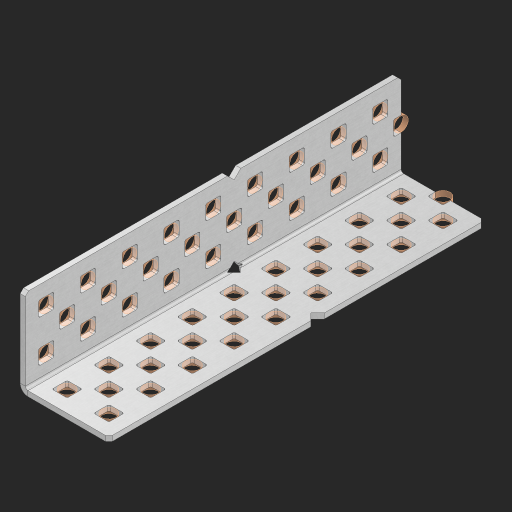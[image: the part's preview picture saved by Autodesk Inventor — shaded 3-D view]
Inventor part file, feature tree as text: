
AUTODESK INVENTOR PART (.ipt)
format: ipt  version: 2023 (Build 270158000, 158)  size: 940,544 bytes
history: native  units: in
note: dims shown in document units (in); Inventor stores cm internally (conversion verified against a paired STEP export)
features: other x60, extrude x52, sheet_metal_op x8, sketch x7, pattern_linear x2, mirror x1, chamfer x1
ambient origin geometry x8: Origin, YZ Plane, XZ Plane, XY Plane, X Axis, Y Axis, Z Axis, Center Point
bodies: Solid1 (feature_tree), Body (feature_tree)
feature tree (131):
  sheet_metal_op  "Flanges"
  sheet_metal_op  "Body Pattern"
  pattern_linear  "Center Pattern"  Spacing1=1.0in  [1 undecoded]
  other  "Arc Length"
  pattern_linear  "Notch Pattern"  Spacing1=0.25in  [1 undecoded]
  other  "Diagonal Plane"
  mirror  "Everything Mirrored"
  chamfer  "End Chamfer"
  sketch  "Sketch1"  dims[d0=1.0in]
  other  "Plate1"
  sketch  "Sketch2"  dims[d1=4.5in]
  other  "Plate2"
  sheet_metal_op  "Bend1"
  sheet_metal_op  "Corner1"
  sketch  "Sketch8"  dims[d2=0.0625in]
  sketch  "Sketch9"  dims[d3=0.0625in]
  other  "Srf91"
  sheet_metal_op  "Body Pattern Sketch"
  other  "Srf92"
  sketch  "Sketch13"  dims[d4=0.0312in]
  sketch  "Sketch15"  dims[d5=0.125in]
  sketch  "Sketch16"  dims[d6=0.0625in d7=1.0in d8=90.0deg d9=0.0312in d10=0.25in d11=0.0625in d12=0.0625in d49=0.182in d50=0.02in d52=0.25in d53=0.0625in d54=0.0in d55=0.172in d56=1.0in d57=0.0in d60=3.5433in d62=0.5in d63=0.7874in d65=0.5in d85=0.1473in d86=0.1782in d89=0.0625in d90=0.0in d91=0.04in d92=0.0491in d95=2.5in d96=0.04in d97=0.25in d98=45.0deg d99=0.25in d106=0.182in d107=0.02in d108=0.5in d110=0.0625in d111=0.0in d112=0.172in d113=0.5in d114=0.0in d117=0.5in d123=0.25in d125=0.25in d126=0.0491in d127=0.1473in d128=0.08in d129=0.04in d130=2.5in]
  other  "Srf786"
  other  "Srf856"
  other  "Srf857"
  other  "Srf858"
  other  "Srf859"
  other  "Srf860"
  other  "Srf861"
  other  "Srf889"
  other  "Srf890"
  other  "Srf891"
  other  "Srf1275"
  other  "Srf1276"
  other  "Srf1278"
  other  "Srf1279"
  other  "Srf1280"
  other  "Srf1281"
  other  "Srf1282"
  other  "Srf1283"
  other  "Srf1277"
  other  "Srf1285"
  other  "Srf1286"
  other  "Srf1287"
  other  "Srf1383"
  other  "Srf1384"
  other  "Srf1385"
  other  "Srf1386"
  other  "Srf1387"
  other  "Srf1388"
  other  "Srf1389"
  other  "Srf1390"
  other  "Srf1391"
  other  "Srf1392"
  other  "Srf1445"
  other  "Srf1446"
  other  "Srf1447"
  other  "Srf1448"
  other  "Srf1449"
  other  "Srf1475"
  other  "Srf1476"
  other  "Srf1477"
  other  "Srf1478"
  other  "Srf1479"
  other  "Srf1480"
  other  "Srf1481"
  other  "Srf1482"
  other  "Srf1483"
  other  "Srf1484"
  other  "Srf1537"
  other  "Srf1538"
  other  "Srf1539"
  other  "Srf1540"
  other  "Srf1541"
  sheet_metal_op  "Body Stamp"
  sheet_metal_op  "Body Circle"
  other  "Center Stamp"
  other  "Center Circle"
  sheet_metal_op  "Notch"
  extrude  "ExtrusionSrf92"  Depth=0.0625in
  extrude  "ExtrusionSrf856"  Depth=0.0625in
  extrude  "ExtrusionSrf857"  Depth=0.182in
  extrude  "ExtrusionSrf858"  Depth=0.02in
  extrude  "ExtrusionSrf859"  Depth=0.25in
  extrude  "ExtrusionSrf860"  Depth=0.0625in
  extrude  "ExtrusionSrf861"  TaperAngle=0.0deg  [1 undecoded]
  extrude  "ExtrusionSrf889"  Depth=2.5in
  extrude  "ExtrusionSrf890"  Depth=1.0in TaperAngle=0.0deg
  extrude  "ExtrusionSrf891"  Depth=2.5in
  extrude  "ExtrusionSrf1275"  Depth=0.5in
  extrude  "ExtrusionSrf1276"  Depth=2.5in
  extrude  "ExtrusionSrf1277"  Depth=2.5in
  extrude  "ExtrusionSrf1278"  Depth=0.0625in
  extrude  "ExtrusionSrf1279"  Depth=2.5in TaperAngle=0.0deg
  extrude  "ExtrusionSrf1280"  Depth=2.5in
  extrude  "ExtrusionSrf1281"  Depth=0.25in TaperAngle=45.0deg
  extrude  "ExtrusionSrf1282"  Depth=0.25in
  extrude  "ExtrusionSrf1345"  Depth=0.182in
  extrude  "ExtrusionSrf1346"  Depth=0.02in
  extrude  "ExtrusionSrf1347"  Depth=0.5in
  extrude  "ExtrusionSrf1348"  Depth=0.0625in
  extrude  "ExtrusionSrf1383"  TaperAngle=0.0deg  [1 undecoded]
  extrude  "ExtrusionSrf1384"  Depth=2.5in
  extrude  "ExtrusionSrf1385"  Depth=0.5in TaperAngle=0.0deg
  extrude  "ExtrusionSrf1386"  Depth=0.5in
  extrude  "ExtrusionSrf1387"  Depth=0.25in
  extrude  "ExtrusionSrf1388"  Depth=0.25in
  extrude  "ExtrusionSrf1389"  Depth=2.5in
  extrude  "ExtrusionSrf1390"  Depth=2.5in
  extrude  "ExtrusionSrf1391"  Depth=2.5in
  extrude  "ExtrusionSrf1392"  Depth=2.5in
  extrude  "ExtrusionSrf1445"  Depth=2.5in
  extrude  "ExtrusionSrf1446"  [1 undecoded]
  extrude  "ExtrusionSrf1447"  [1 undecoded]
  extrude  "ExtrusionSrf1448"  [1 undecoded]
  extrude  "ExtrusionSrf1449"  [1 undecoded]
  extrude  "ExtrusionSrf1475"  [1 undecoded]
  extrude  "ExtrusionSrf1476"  [1 undecoded]
  extrude  "ExtrusionSrf1477"  [1 undecoded]
  extrude  "ExtrusionSrf1478"  [1 undecoded]
  extrude  "ExtrusionSrf1479"  [1 undecoded]
  extrude  "ExtrusionSrf1480"  [1 undecoded]
  extrude  "ExtrusionSrf1481"  [1 undecoded]
  extrude  "ExtrusionSrf1482"  [1 undecoded]
  extrude  "ExtrusionSrf1483"  [1 undecoded]
  extrude  "ExtrusionSrf1484"  [1 undecoded]
  extrude  "ExtrusionSrf1537"  [1 undecoded]
  extrude  "ExtrusionSrf1538"  [1 undecoded]
  extrude  "ExtrusionSrf1539"  [1 undecoded]
  extrude  "ExtrusionSrf1540"  [1 undecoded]
  extrude  "ExtrusionSrf1541"  [1 undecoded]
note: 23 required parameter values undecoded (feature->parameter linkage not recoverable at this tier; creation-order binding heuristic only, values carry confidence <= 0.55)
